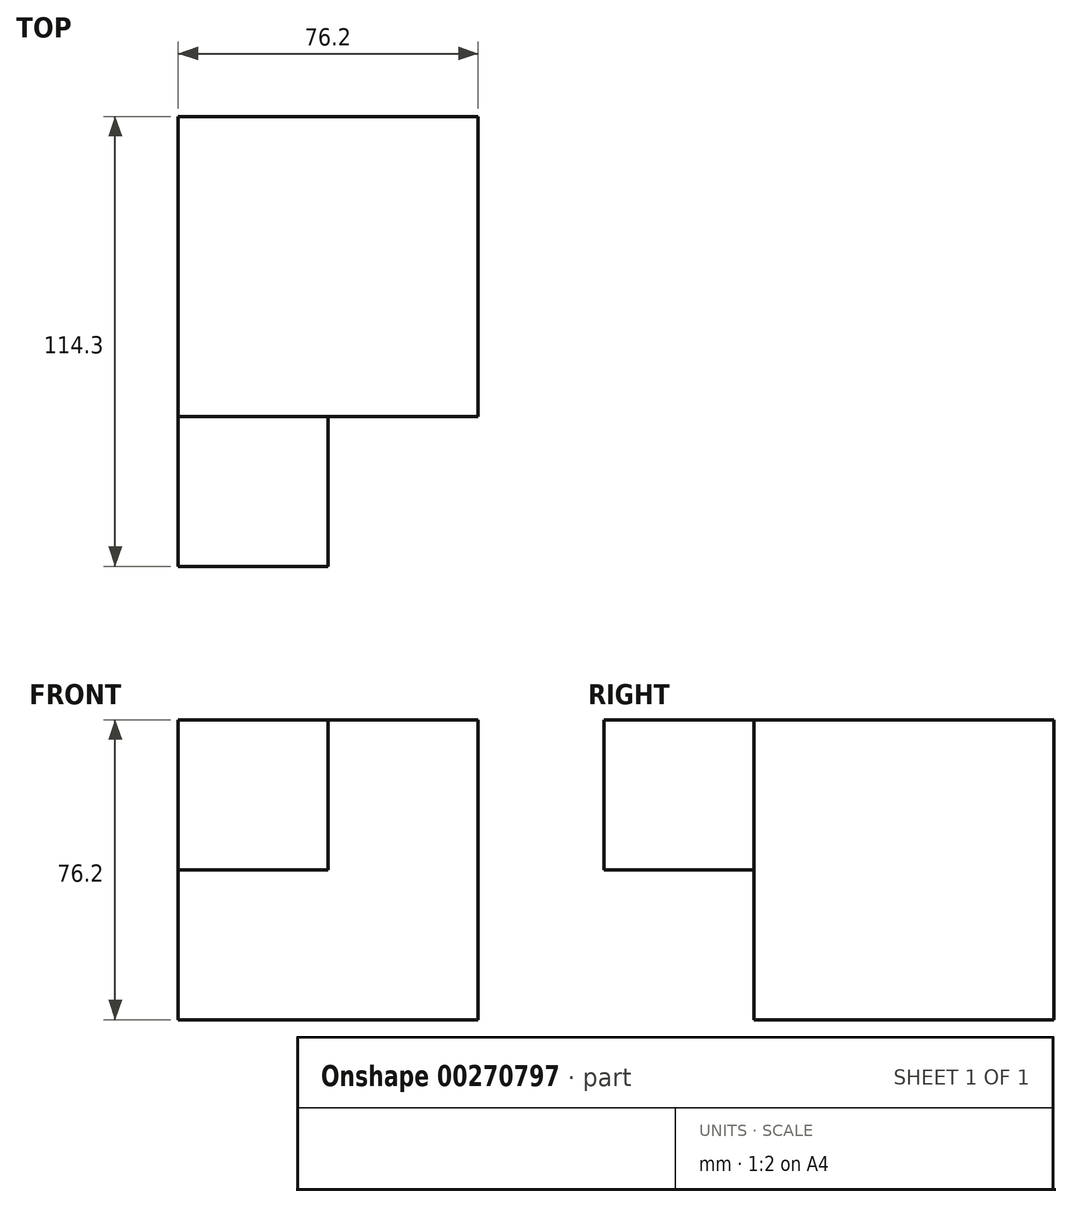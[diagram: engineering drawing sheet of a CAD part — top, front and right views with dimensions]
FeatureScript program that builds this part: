
annotation { "Feature Type Name" : "Feature", "Feature Type Description" : "" }
export const myFeature = defineFeature(function(context is Context, id is Id, definition is map)
    precondition{}
    {
        {
            var Q0;
            Q0=qCreatedBy(makeId("Front.planeOp"),FACE);
            var sketch = newSketch(context, id + "F0", { "sketchPlane" : qUnion([Q0])});
            skLineSegment(sketch, "E0.bottom", {"start": v(-34.32, 51.42) * mm, "end": v(41.88, 51.42) * mm});
            skLineSegment(sketch, "E0.top", {"start": v(-34.32, -24.78) * mm, "end": v(41.88, -24.78) * mm});
            skLineSegment(sketch, "E0.left", {"start": v(-34.32, 51.42) * mm, "end": v(-34.32, -24.78) * mm});
            skLineSegment(sketch, "E0.right", {"start": v(41.88, 51.42) * mm, "end": v(41.88, -24.78) * mm});
            skSolve(sketch);
        }
        {
            var Q0;
            Q0 = qSketchRegion(id + "F0", true);
            extrude(context, id + "F1", {"entities" : qUnion([Q0]), "depth" : 76.2 * mm});
        }
        {
            var Q0;
            Q0=makeQuery(id+"F1.opExtrude","CAP_FACE",FACE,{"disambiguationData":[OSD([sQuery(id+"F0.wireOp",EDGE,"E0.bottom"),sQuery(id+"F0.wireOp",EDGE,"E0.top"),sQuery(id+"F0.wireOp",EDGE,"E0.left"),sQuery(id+"F0.wireOp",EDGE,"E0.right")])],"isStart":false});
            var sketch = newSketch(context, id + "F2", { "sketchPlane" : qUnion([Q0])});
            skLineSegment(sketch, "E1.bottom", {"start": v(-34.32, 51.42) * mm, "end": v(3.78, 51.42) * mm});
            skLineSegment(sketch, "E1.top", {"start": v(-34.32, 13.32) * mm, "end": v(3.78, 13.32) * mm});
            skLineSegment(sketch, "E1.left", {"start": v(-34.32, 51.42) * mm, "end": v(-34.32, 13.32) * mm});
            skLineSegment(sketch, "E1.right", {"start": v(3.78, 51.42) * mm, "end": v(3.78, 13.32) * mm});
            skSolve(sketch);
        }
        {
            var Q0;
            Q0 = qSketchRegion(id + "F2", true);
            extrude(context, id + "F3", {"entities" : qUnion([Q0]), "depth" : 38.1 * mm});
        }
    });
